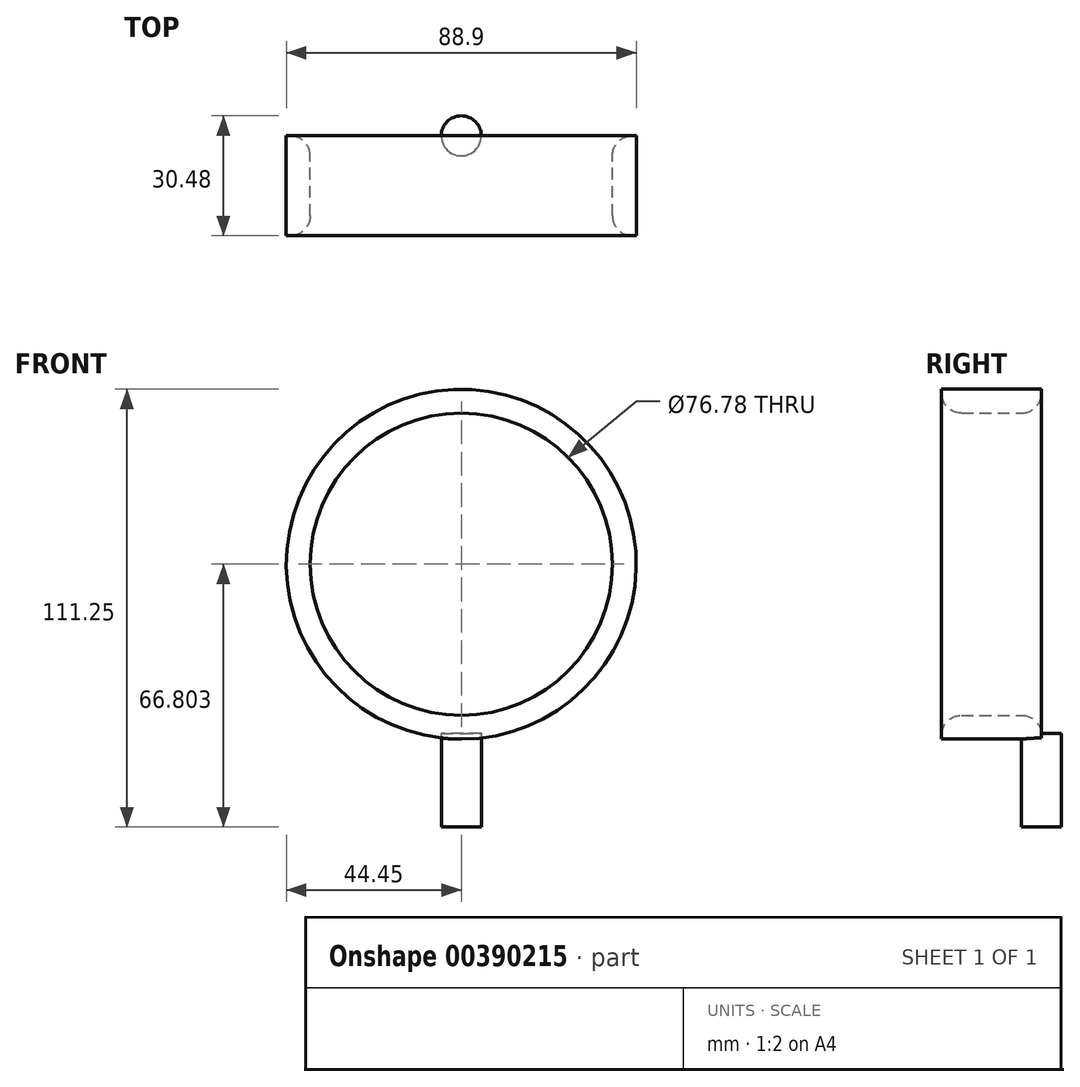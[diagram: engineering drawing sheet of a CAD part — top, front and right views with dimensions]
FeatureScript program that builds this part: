
annotation { "Feature Type Name" : "Feature", "Feature Type Description" : "" }
export const myFeature = defineFeature(function(context is Context, id is Id, definition is map)
    precondition{}
    {
        {
            var Q0;
            Q0=qCreatedBy(makeId("Front.planeOp"),FACE);
            var sketch = newSketch(context, id + "F0", { "sketchPlane" : qUnion([Q0])});
            skCircle(sketch, "E0", {"center": v(0, 43) * mm, "radius": 44.45 * mm});
            skCircle(sketch, "E1", {"center": v(0, 43) * mm, "radius": 38.4 * mm});
            skSolve(sketch);
        }
        {
            var Q0;
            Q0=qSketchRegion(id+"F0",true);
            extrude(context, id + "F1", {"entities" : qUnion([Q0]), "depth" : 25.4 * mm});
        }
        {
            var Q0;
            Q0=makeQuery(id+"F1.opExtrude","CAP_EDGE",EDGE,{"disambiguationData":[OSD([sQuery(id+"F0.wireOp",EDGE,"E1")])],"isStart":false});
            var Q1;
            Q1=makeQuery(id+"F1.opExtrude","CAP_EDGE",EDGE,{"disambiguationData":[OSD([sQuery(id+"F0.wireOp",EDGE,"E1")])],"isStart":true});
            fillet(context, id + "F2", {"entities" : qUnion([Q0, Q1]), "radius" : 5.08 * mm, "tangentPropagation" : true, "allowEdgeOverflow" : false});
        }
        {
            var Q0;
            Q0=qCreatedBy(makeId("Front.planeOp"),FACE);
            var sketch = newSketch(context, id + "F3", { "sketchPlane" : qUnion([Q0])});
            skLineSegment(sketch, "E2.bottom", {"start": v(0, 0) * mm, "end": v(-5.08, 0) * mm});
            skLineSegment(sketch, "E2.top", {"start": v(0, -23.8) * mm, "end": v(-5.08, -23.8) * mm});
            skLineSegment(sketch, "E2.left", {"start": v(0, 0) * mm, "end": v(0, -23.8) * mm});
            skLineSegment(sketch, "E2.right", {"start": v(-5.08, 0) * mm, "end": v(-5.08, -23.8) * mm});
            skSolve(sketch);
        }
        {
            var Q0;
            Q0=qSketchRegion(id+"F3",true);
            var Q1;
            Q1=sQuery(id+"F3.wireOp",EDGE,"E2.left");
            revolve(context, id + "F4", {"operationType" : NewBodyOperationType.ADD, "entities" : qUnion([Q0]), "axis" : qUnion([Q1]), "revolveType" : RevolveType.FULL});
        }
    });
